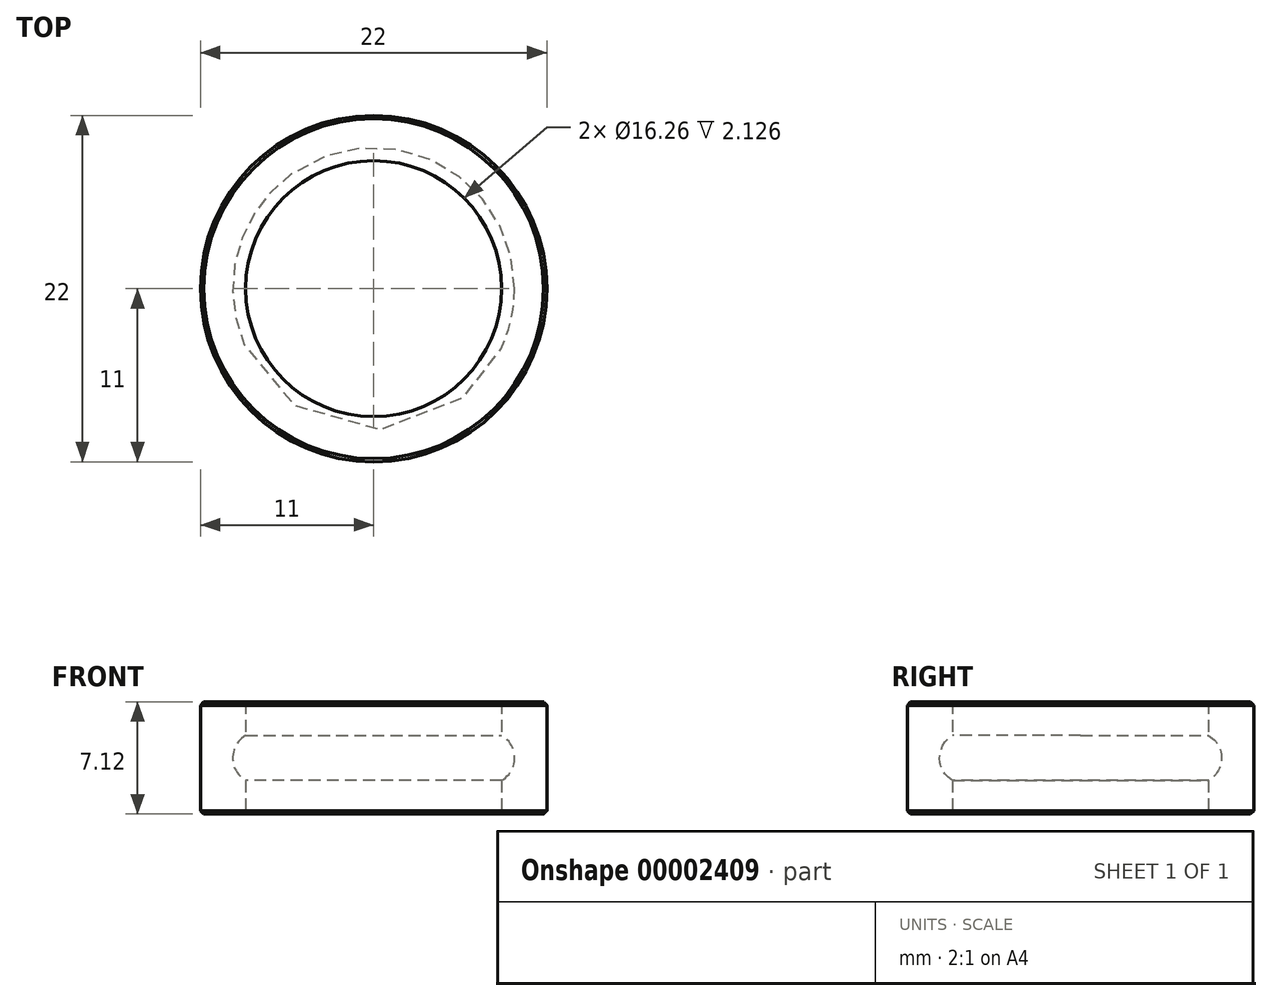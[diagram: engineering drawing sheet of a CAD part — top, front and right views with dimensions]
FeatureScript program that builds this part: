
annotation { "Feature Type Name" : "Feature", "Feature Type Description" : "" }
export const myFeature = defineFeature(function(context is Context, id is Id, definition is map)
    precondition{}
    {
        {
            var Q0;
            Q0=qCreatedBy(makeId("Top.planeOp"),FACE);
            var sketch = newSketch(context, id + "F0", { "sketchPlane" : qUnion([Q0])});
            skCircle(sketch, "E0", {"center": v(0, 0) * mm, "radius": 11 * mm});
            skCircle(sketch, "E1", {"center": v(0, 0) * mm, "radius": 8.13 * mm});
            skSolve(sketch);
        }
        {
            var Q0;
            Q0=qSketchRegion(id+"F0",true);
            extrude(context, id + "F1", {"entities" : qUnion([Q0]), "endBound" : BoundingType.SYMMETRIC, "depth" : 7.11 * mm});
        }
        {
            var Q0;
            Q0=makeQuery(id+"F1.opExtrude","CAP_EDGE",EDGE,{"disambiguationData":[OSD([sQuery(id+"F0.wireOp",EDGE,"E0")])],"isStart":false});
            var Q1;
            Q1=makeQuery(id+"F1.opExtrude","CAP_EDGE",EDGE,{"disambiguationData":[OSD([sQuery(id+"F0.wireOp",EDGE,"E0")])],"isStart":true});
            chamfer(context, id + "F2", {"entities" : qUnion([Q0, Q1]), "width" : 0.2 * mm, "tangentPropagation" : true});
        }
        {
            var Q0;
            Q0=qCreatedBy(makeId("Right.planeOp"),FACE);
            var sketch = newSketch(context, id + "F3", { "sketchPlane" : qUnion([Q0])});
            skArc(sketch, "E2", {"start": v(7.3, -1.65) * mm, "mid": v(8.95, 0) * mm, "end": v(7.3, 1.65) * mm});
            skLineSegment(sketch, "E3", {"start": v(7.3, 1.65) * mm, "end": v(7.3, -1.65) * mm});
            skLineSegment(sketch, "E4", {"start": v(0, 0) * mm, "end": v(0, 4.16) * mm, "construction": true});
            skSolve(sketch);
        }
        {
            var Q0;
            Q0=qSketchRegion(id+"F3",true);
            var Q1;
            Q1=sQuery(id+"F3.wireOp",EDGE,"E2");
            var Q2;
            Q2=sQuery(id+"F3.wireOp",EDGE,"E3");
            var Q3;
            Q3=sQuery(id+"F3.wireOp",EDGE,"E4");
            revolve(context, id + "F4", {"operationType" : NewBodyOperationType.REMOVE, "entities" : qUnion([Q0]), "surfaceEntities" : qUnion([Q1, Q2]), "axis" : qUnion([Q3]), "revolveType" : RevolveType.FULL, "oppositeDirection" : true});
        }
    });
